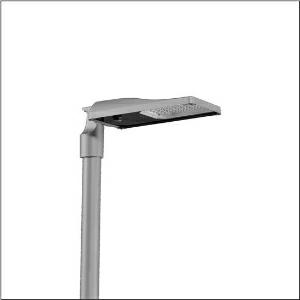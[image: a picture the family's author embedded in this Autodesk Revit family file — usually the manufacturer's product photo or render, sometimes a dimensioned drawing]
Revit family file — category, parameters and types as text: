
# Revit family: streetlight_sl_31_mini___st1_0a_5xh6d31r08ga_9a85
name_source: partatom
category: Lighting Fixtures
units: mm (PartAtom-declared; Revit-internal decimal feet)

## family parameters
Cut with Voids When Loaded = No
Host = Face
Light Source = No
Part Type = Normal
Room Calculation Point = No
Round Connector Dimension = Use Diameter
Shared = No

## types (1)
- --- (1 x LED, 5880 lm, 39.3 W, 3000K)
    Apparent Load = 39 VA
    CIE Flux Codes = 37 72 97 100 100
    Color Rendering = 70
    Color Temperature = 3000K
    Default Elevation = 1800 mm
    Description = Streetlight SL 31 mini D4i, Desk-Remote mast luminaire for post-top, side-entry; light control with lens of PMMA; light distribution: ST1.0a, direct asymmetric distribution, for standard-compliant lighting for roads and squares; LED: luminous flux: 5.880lm, light colour: 730, colour temperature: 3000K; luminous efficacy: 149,6lm/W; control: pre-setting: logarithmic dimming characteristic, flexible luminous flux parameterisation, time-dependent luminous flux control, constant luminous flux control, power reduction, intelligent temperature release in ECG and LED module, overheat protection; luminaire housing, of diecast aluminium, SITECO metallic grey (DB 702S), corrosivity category C5 high according to DIN EN ISO 12944; cover of toughened safety glass, transparent, opened without tools; mast flange of diecast aluminium, SITECO metallic grey (DB 702S), spigot size: 76/60mm, mast flange included unmounted; with cable H07RN-F 2x 1.5mm², cable length: 6,5m, connection cable pre-assembled; mains connection: 220..240V, AC, 50/60Hz; power consumption (at start of service life): 39,3W / (at end of service life): 40,7W / (with reduced operation 50%): 18,1W; protection rating (complete): IP66; insulation class (complete): insulation class II (safety insulation); impact resistance: IK09; certification: CE, ENEC, ENEC+, VDE, UKCA, ZD4i; permissible operating ambient temperature for outdoor applications: -40..+50°C; packaging unit: 1 piece

Light Distribution: ST1.0a
    Height = 76 mm
    Lamp = 1 x LED
    Lamp Light Flux = 5880 lm
    Lamp Power = 39.3 W
    Lamp count = 1
    Length = 547 mm
    Luminous efficacy = 150 lm/W
    Manufacturer = Siteco
    ModVariant = No
    Model = 5XH6D31R08GA
    Number of Poles = 1
    OnlyDefault = Yes
    Power Factor = 1
    Product Name = Streetlight SL 31 mini | ST1.0a
    Product group = mast luminaire | pylon top
    ProductGroupID = 6100
    Protection Class = Protection class II
    Protection Degree = IP 66
    RLX_Detail_Level = 1
    RLX_Emergency_Light_Flux = 0 lm
    RLX_Emergency_Type = 0
    RLX_Emergency_Type_DB = No
    RlxData = <blob elided: 39809 chars, md5=968f44d5>
    Socket = socket
    Standby Power = 0 W
    System Light Flux = 5880 lm
    System Power = 39 W
    Type Comments = factory setting: luminous flux: 100 % | dim-lin: 254 | 798 mA
    Type Image = l_1300328.jpg
    URL = http://relux.com
    VarID = @adj_060785
    Voltage = 0 V
    Weight = 0.00 kg
    Width = 265 mm

## geometry (parser evidence)
native form markers: Blend x4, Sweep x9
no freeform markers — native parametric forms only
